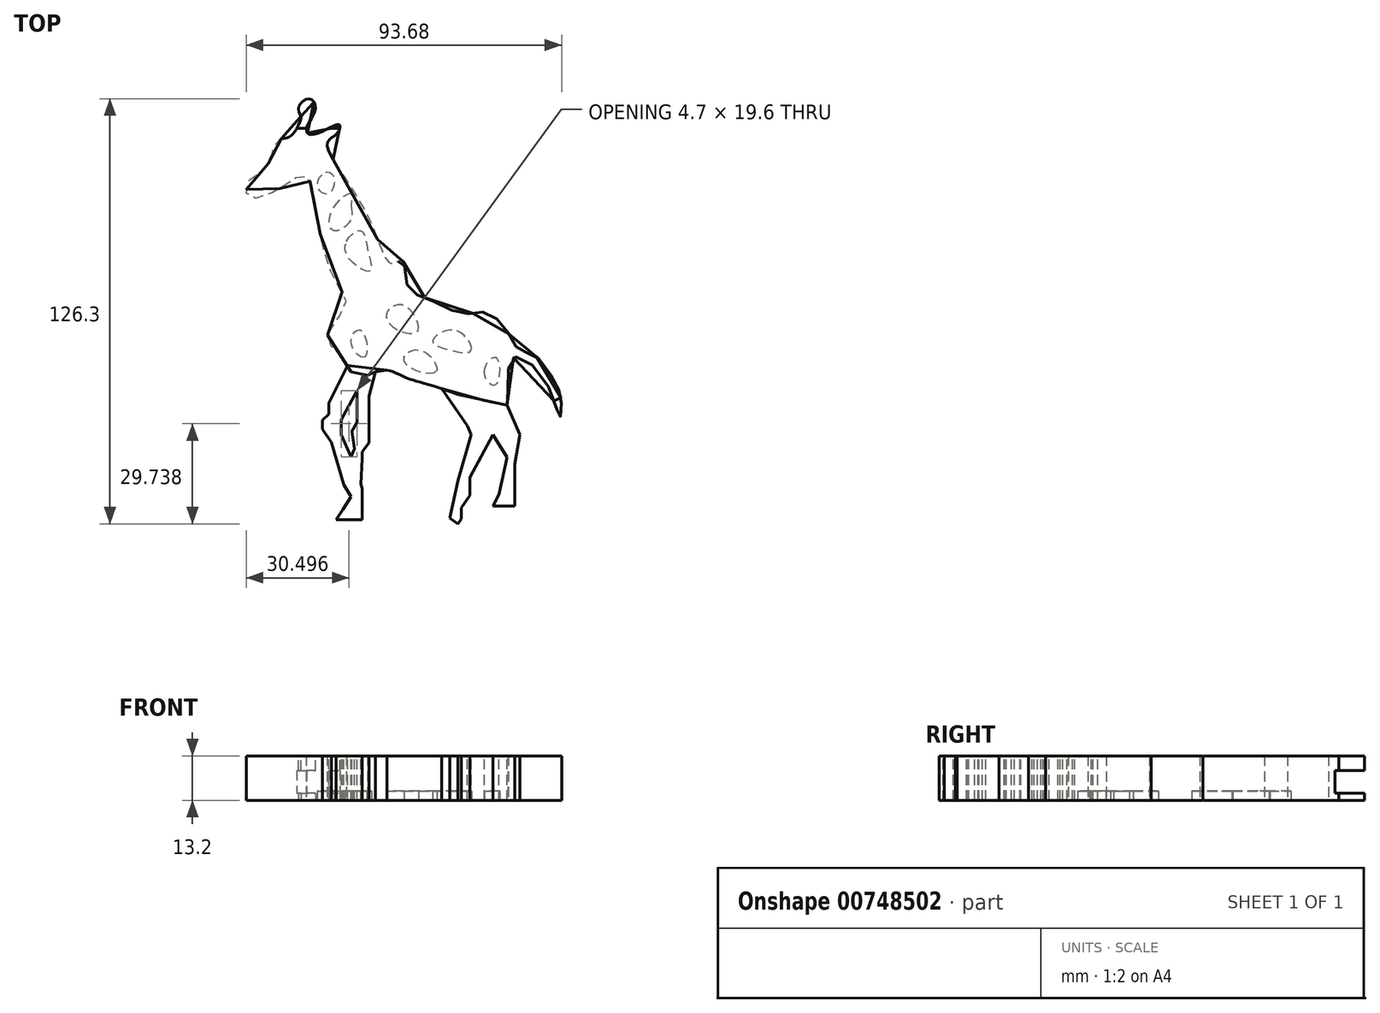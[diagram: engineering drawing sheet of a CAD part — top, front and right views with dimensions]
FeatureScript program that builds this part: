
annotation { "Feature Type Name" : "Feature", "Feature Type Description" : "" }
export const myFeature = defineFeature(function(context is Context, id is Id, definition is map)
    precondition{}
    {
        {
            var Q0;
            Q0=qCreatedBy(makeId("Top.planeOp"),FACE);
            var sketch = newSketch(context, id + "F0", { "sketchPlane" : qUnion([Q0])});
            skFitSpline(sketch, "E0", {"points": [v(-70.24, 39.72) * mm, v(-69.58, 45) * mm, v(-66.5, 46.77) * mm, v(-63.63, 50.95) * mm, v(-62.53, 54.25) * mm, v(-61.21, 56.68) * mm, v(-57.9, 57.56) * mm, v(-54.83, 61.96) * mm, v(-54.6, 63.72) * mm, v(-55.27, 66.14) * mm, v(-52.18, 68.79) * mm, v(-50.2, 66.14) * mm, v(-52.62, 60.64) * mm, v(-52.62, 58.66) * mm, v(-49.76, 58.44) * mm, v(-43.16, 61.08) * mm, v(-43.82, 58.44) * mm, v(-46.68, 55.57) * mm, v(-34.79, 34.22) * mm, v(-27.52, 19.9) * mm, v(-24.44, 20.79) * mm, v(-22.68, 12.86) * mm, v(-16.73, 9.34) * mm, v(-6.16, 4.93) * mm, v(0, 5.37) * mm, v(6.6, 0) * mm, v(10.35, -5.86) * mm, v(14.53, -7.18) * mm, v(21.14, -15.76) * mm, v(22.9, -21.27) * mm, v(22.46, -25.9) * mm, v(18.72, -16.2) * mm, v(8.8, -8.06) * mm, v(7.05, -18.19) * mm, v(5.95, -22.81) * mm, v(-13.43, -17.09) * mm, v(-22.9, -14.22) * mm, v(-29.5, -11.8) * mm, v(-34.57, -13.34) * mm, v(-38.31, -13.78) * mm, v(-42.5, -7.62) * mm, v(-46.68, -2.11) * mm, v(-41.17, 7.57) * mm, v(-43.6, 13.3) * mm, v(-48.88, 28.93) * mm, v(-50.86, 41.48) * mm, v(-53.28, 45.89) * mm, v(-57.9, 44.13) * mm, v(-63.63, 40.6) * mm, v(-70.24, 39.72) * mm]});
            skSolve(sketch);
        }
        {
            var Q0;
            Q0 = qSketchRegion(id + "F0", true);
            extrude(context, id + "F1", {"entities" : qUnion([Q0]), "depth" : 13.2 * mm, "offsetDistance" : 25 * mm});
        }
        {
            var Q0;
            Q0=qCreatedBy(makeId("Right.planeOp"),FACE);
            var sketch = newSketch(context, id + "F2", { "sketchPlane" : qUnion([Q0])});
            skLineSegment(sketch, "E1", {"start": v(84.33, -7.6) * mm, "end": v(77.94, 2.1) * mm});
            skLineSegment(sketch, "E2", {"start": v(77.94, 2.1) * mm, "end": v(60.06, 2.1) * mm});
            skLineSegment(sketch, "E3", {"start": v(60.06, 2.1) * mm, "end": v(60.06, 8.92) * mm});
            skLineSegment(sketch, "E4", {"start": v(60.06, 8.92) * mm, "end": v(81.47, 8.92) * mm});
            skLineSegment(sketch, "E5", {"start": v(81.47, 8.92) * mm, "end": v(84.33, -7.6) * mm});
            skSolve(sketch);
        }
        {
            var Q0;
            Q0 = qSketchRegion(id + "F2", true);
            extrude(context, id + "F3", {"entities" : qUnion([Q0]), "operationType" : NewBodyOperationType.REMOVE, "oppositeDirection" : true, "depth" : 75.9 * mm, "offsetDistance" : 25 * mm});
        }
        {
            var Q0;
            Q0=makeQuery(id+"F1.opExtrude","CAP_FACE",FACE,{"disambiguationData":[OSD([sQuery(id+"F0.wireOp",EDGE,"E0")])],"isStart":false});
            var sketch = newSketch(context, id + "F4", { "sketchPlane" : qUnion([Q0])});
            skLineSegment(sketch, "E6", {"start": v(-60.8, -7.84) * mm, "end": v(12.52, -23.47) * mm});
            skLineSegment(sketch, "E7", {"start": v(12.52, -23.47) * mm, "end": v(7.65, -46.33) * mm});
            skLineSegment(sketch, "E8", {"start": v(7.65, -46.33) * mm, "end": v(-61.24, -14.23) * mm});
            skLineSegment(sketch, "E9", {"start": v(-61.24, -14.23) * mm, "end": v(-60.8, -7.84) * mm});
            skSolve(sketch);
        }
        {
            var Q0;
            Q0 = qSketchRegion(id + "F4", true);
            extrude(context, id + "F5", {"entities" : qUnion([Q0]), "operationType" : NewBodyOperationType.REMOVE, "oppositeDirection" : true, "depth" : 25 * mm, "offsetDistance" : 25 * mm});
        }
        {
            var Q0;
            Q0=makeQuery(id+"F5.boolean.opBoolean","COPY",FACE,{"disambiguationData":[OD(1.0)],"derivedFrom":makeQuery(id+"F5.opExtrude","SWEPT_FACE",FACE,{"disambiguationData":[OSD([sQuery(id+"F4.wireOp",EDGE,"E6")])]})});
            var sketch = newSketch(context, id + "F6", { "sketchPlane" : qUnion([Q0])});
            skEllipse(sketch, "E10", {"center": v(2.03, 10.01) * mm, "majorRadius": 6.39 * mm, "minorRadius": 1.84 * mm, "majorAxis": v(1, 0)});
            skSolve(sketch);
        }
        {
            var Q0;
            Q0=qCreatedBy(makeId("Top.planeOp"),FACE);
            var sketch = newSketch(context, id + "F7", { "sketchPlane" : qUnion([Q0])});
            skFitSpline(sketch, "E11", {"points": [v(-14.2, -17.08) * mm, v(-8.6, -24.71) * mm, v(-4.55, -30) * mm, v(-5.17, -33.74) * mm, v(-6.57, -37.8) * mm, v(-8.6, -46.82) * mm, v(-12.02, -48.53) * mm, v(-21.68, -45.42) * mm, v(-22.61, -43.08) * mm, v(-25.26, -35.77) * mm, v(-24.17, -33.12) * mm, v(-14.2, -17.08) * mm]});
            skSolve(sketch);
        }
        {
            var Q0;
            Q0=makeQuery(id+"F1.opExtrude","CAP_FACE",FACE,{"disambiguationData":[OSD([sQuery(id+"F0.wireOp",EDGE,"E0")])],"isStart":false});
            var sketch = newSketch(context, id + "F8", { "sketchPlane" : qUnion([Q0])});
            skLineSegment(sketch, "E12", {"start": v(-40.68, -10.45) * mm, "end": v(-46.28, -21.65) * mm});
            skLineSegment(sketch, "E13", {"start": v(-46.28, -21.65) * mm, "end": v(-46.28, -24.91) * mm});
            skLineSegment(sketch, "E14", {"start": v(-46.28, -24.91) * mm, "end": v(-48.12, -26.75) * mm});
            skLineSegment(sketch, "E15", {"start": v(-48.12, -26.75) * mm, "end": v(-48.12, -29.4) * mm});
            skLineSegment(sketch, "E16", {"start": v(-48.12, -29.4) * mm, "end": v(-45.46, -33.29) * mm});
            skLineSegment(sketch, "E17", {"start": v(-45.46, -33.29) * mm, "end": v(-41.79, -45.95) * mm});
            skLineSegment(sketch, "E18", {"start": v(-41.79, -45.95) * mm, "end": v(-39.6, -49.42) * mm});
            skLineSegment(sketch, "E19", {"start": v(-39.6, -49.42) * mm, "end": v(-41.99, -53.3) * mm});
            skLineSegment(sketch, "E20", {"start": v(-41.99, -53.3) * mm, "end": v(-44.03, -56.36) * mm});
            skLineSegment(sketch, "E21", {"start": v(-44.03, -56.36) * mm, "end": v(-36.27, -56.36) * mm});
            skLineSegment(sketch, "E22", {"start": v(-36.27, -56.36) * mm, "end": v(-36.27, -46.97) * mm});
            skLineSegment(sketch, "E23", {"start": v(-36.27, -46.97) * mm, "end": v(-36.72, -45.7) * mm});
            skLineSegment(sketch, "E24", {"start": v(-39.6, -37.57) * mm, "end": v(-42.6, -31.04) * mm});
            skLineSegment(sketch, "E25", {"start": v(-42.6, -31.04) * mm, "end": v(-42.6, -26.55) * mm});
            skLineSegment(sketch, "E26", {"start": v(-42.6, -26.55) * mm, "end": v(-37.9, -17.97) * mm});
            skLineSegment(sketch, "E27", {"start": v(-32.36, -12.36) * mm, "end": v(-28.92, -11.86) * mm});
            skLineSegment(sketch, "E28", {"start": v(-28.92, -11.86) * mm, "end": v(-40.68, -10.45) * mm});
            skLineSegment(sketch, "E29", {"start": v(-10.34, -55.75) * mm, "end": v(-7.83, -57.5) * mm});
            skLineSegment(sketch, "E30", {"start": v(-7.83, -57.5) * mm, "end": v(-6.83, -56.08) * mm});
            skLineSegment(sketch, "E31", {"start": v(-6.83, -56.08) * mm, "end": v(-6.83, -52.69) * mm});
            skLineSegment(sketch, "E32", {"start": v(-6.83, -52.69) * mm, "end": v(-4.3, -49.09) * mm});
            skLineSegment(sketch, "E33", {"start": v(-4.3, -49.09) * mm, "end": v(-4.3, -43.7) * mm});
            skLineSegment(sketch, "E34", {"start": v(-4.3, -43.7) * mm, "end": v(2.53, -31.04) * mm});
            skLineSegment(sketch, "E35", {"start": v(6.76, -37.78) * mm, "end": v(2.53, -31.04) * mm});
            skLineSegment(sketch, "E36", {"start": v(6.76, -37.78) * mm, "end": v(4.37, -48.8) * mm});
            skLineSegment(sketch, "E37", {"start": v(4.37, -48.8) * mm, "end": v(2.53, -52.2) * mm});
            skLineSegment(sketch, "E38", {"start": v(2.53, -52.2) * mm, "end": v(9.06, -52.2) * mm});
            skLineSegment(sketch, "E39", {"start": v(9.06, -52.2) * mm, "end": v(9.06, -48.4) * mm});
            skLineSegment(sketch, "E40", {"start": v(9.06, -48.4) * mm, "end": v(9.06, -39.82) * mm});
            skLineSegment(sketch, "E41", {"start": v(9.06, -39.82) * mm, "end": v(10.5, -31.04) * mm});
            skLineSegment(sketch, "E42", {"start": v(10.5, -31.04) * mm, "end": v(6.76, -22.25) * mm});
            skLineSegment(sketch, "E43", {"start": v(6.76, -22.25) * mm, "end": v(0, -20.8) * mm});
            skLineSegment(sketch, "E44", {"start": v(0, -20.8) * mm, "end": v(-12.7, -17.34) * mm});
            skLineSegment(sketch, "E45", {"start": v(-12.7, -17.34) * mm, "end": v(-5.03, -28.38) * mm});
            skLineSegment(sketch, "E46", {"start": v(-5.03, -28.38) * mm, "end": v(-3.9, -31.04) * mm});
            skLineSegment(sketch, "E47", {"start": v(-3.9, -31.04) * mm, "end": v(-7.83, -44.72) * mm});
            skLineSegment(sketch, "E48", {"start": v(-7.83, -44.72) * mm, "end": v(-10.34, -55.75) * mm});
            skLineSegment(sketch, "E49", {"start": v(-36.72, -45.7) * mm, "end": v(-36.27, -38.19) * mm});
            skLineSegment(sketch, "E50", {"start": v(-36.27, -38.19) * mm, "end": v(-36.27, -36.14) * mm});
            skLineSegment(sketch, "E51", {"start": v(-36.27, -36.14) * mm, "end": v(-34.23, -33.49) * mm});
            skLineSegment(sketch, "E52", {"start": v(-34.23, -33.49) * mm, "end": v(-34.23, -30.02) * mm});
            skLineSegment(sketch, "E53", {"start": v(-34.23, -30.02) * mm, "end": v(-34.23, -27.77) * mm});
            skLineSegment(sketch, "E54", {"start": v(-34.23, -27.77) * mm, "end": v(-34.23, -19.6) * mm});
            skLineSegment(sketch, "E55", {"start": v(-34.23, -19.6) * mm, "end": v(-32.36, -12.36) * mm});
            skLineSegment(sketch, "E56", {"start": v(-37.9, -17.97) * mm, "end": v(-37.9, -22.26) * mm});
            skPoint(sketch, "E56.endSnap0", {"position": v(-40.25, -22.26) * mm});
            skLineSegment(sketch, "E57", {"start": v(-37.9, -22.26) * mm, "end": v(-37.9, -27.36) * mm});
            skLineSegment(sketch, "E58", {"start": v(-37.9, -27.36) * mm, "end": v(-39.36, -30.02) * mm});
            skLineSegment(sketch, "E59", {"start": v(-39.36, -30.02) * mm, "end": v(-38.6, -35.17) * mm});
            skLineSegment(sketch, "E60", {"start": v(-38.6, -35.17) * mm, "end": v(-39.6, -37.57) * mm});
            skPoint(sketch, "E61.orphan", {"position": v(0, -19.13) * mm});
            skPoint(sketch, "E62.start.orphan", {"position": v(2.53, -26.55) * mm});
            skSolve(sketch);
        }
        {
            var Q0;
            Q0 = qSketchRegion(id + "F8", true);
            var Q1;
            Q1=makeQuery(id+"F1.opExtrude","CAP_FACE",FACE,{"disambiguationData":[OSD([sQuery(id+"F0.wireOp",EDGE,"E0")])],"isStart":true});
            extrude(context, id + "F9", {"entities" : qUnion([Q0]), "endBound" : BoundingType.UP_TO_SURFACE, "oppositeDirection" : true, "depth" : 25 * mm, "endBoundEntityFace" : qUnion([Q1]), "offsetDistance" : 25 * mm});
        }
        {
            var Q0;
            Q0=makeQuery(id+"F1.opExtrude","CAP_FACE",FACE,{"disambiguationData":[OSD([sQuery(id+"F0.wireOp",EDGE,"E0")])],"isStart":true});
            var sketch = newSketch(context, id + "F10", { "sketchPlane" : qUnion([Q0])});
            skFitSpline(sketch, "E63", {"points": [v(-3.92, 5.94) * mm, v(-8.76, 0) * mm, v(-15.35, 3.16) * mm, v(-10.95, 5.65) * mm, v(-3.92, 5.94) * mm]});
            skFitSpline(sketch, "E64", {"points": [v(-19.74, 0) * mm, v(-23.99, -7.38) * mm, v(-29.11, -4.9) * mm, v(-25.45, 0) * mm, v(-19.74, 0) * mm]});
            skFitSpline(sketch, "E65", {"points": [v(-40.97, -26.42) * mm, v(-36.73, -29.64) * mm, v(-34.53, -23.2) * mm, v(-33.94, -17.64) * mm, v(-39.6, -20.56) * mm, v(-40.97, -26.42) * mm]});
            skSolve(sketch);
        }
        {
            var Q0;
            Q0 = qSketchRegion(id + "F10", true);
            extrude(context, id + "F11", {"entities" : qUnion([Q0]), "operationType" : NewBodyOperationType.REMOVE, "oppositeDirection" : true, "depth" : 2.8 * mm, "offsetDistance" : 25 * mm});
        }
        {
            var Q0;
            Q0=makeQuery(id+"F1.opExtrude","CAP_FACE",FACE,{"disambiguationData":[OSD([sQuery(id+"F0.wireOp",EDGE,"E0")])],"isStart":true});
            var sketch = newSketch(context, id + "F12", { "sketchPlane" : qUnion([Q0])});
            skFitSpline(sketch, "E66", {"points": [v(-35.6, 7.87) * mm, v(-39.6, 3.47) * mm, v(-36.65, 0) * mm, v(-35.6, 7.87) * mm]});
            skFitSpline(sketch, "E67", {"points": [v(-14.46, 12.36) * mm, v(-23.8, 9.26) * mm, v(-19.11, 5.89) * mm, v(-14.46, 12.36) * mm]});
            skFitSpline(sketch, "E68", {"points": [v(-39.6, -37.19) * mm, v(-39.6, -32.9) * mm, v(-44.68, -29.53) * mm, v(-45.43, -35.3) * mm, v(-39.6, -40.67) * mm, v(-39.6, -37.19) * mm]});
            skFitSpline(sketch, "E69", {"points": [v(-47.2, -46.92) * mm, v(-44.79, -45.5) * mm, v(-46.29, -40.55) * mm, v(-49.55, -42.78) * mm, v(-47.2, -46.92) * mm]});
            skFitSpline(sketch, "E70", {"points": [v(0, 12.36) * mm, v(3.5, 8.16) * mm, v(3.28, 16.22) * mm, v(0, 12.36) * mm]});
            skSolve(sketch);
        }
        {
            var Q0;
            Q0 = qSketchRegion(id + "F12", true);
            var Q1;
            Q1=makeQuery(id+"F11.boolean.opBoolean","COPY",FACE,{"derivedFrom":makeQuery(id+"F11.opExtrude","CAP_FACE",FACE,{"disambiguationData":[OSD([sQuery(id+"F10.wireOp",EDGE,"E65")])],"isStart":false})});
            extrude(context, id + "F13", {"entities" : qUnion([Q0]), "operationType" : NewBodyOperationType.REMOVE, "endBound" : BoundingType.UP_TO_SURFACE, "oppositeDirection" : true, "depth" : 4.2 * mm, "endBoundEntityFace" : qUnion([Q1]), "offsetDistance" : 25 * mm});
        }
    });
